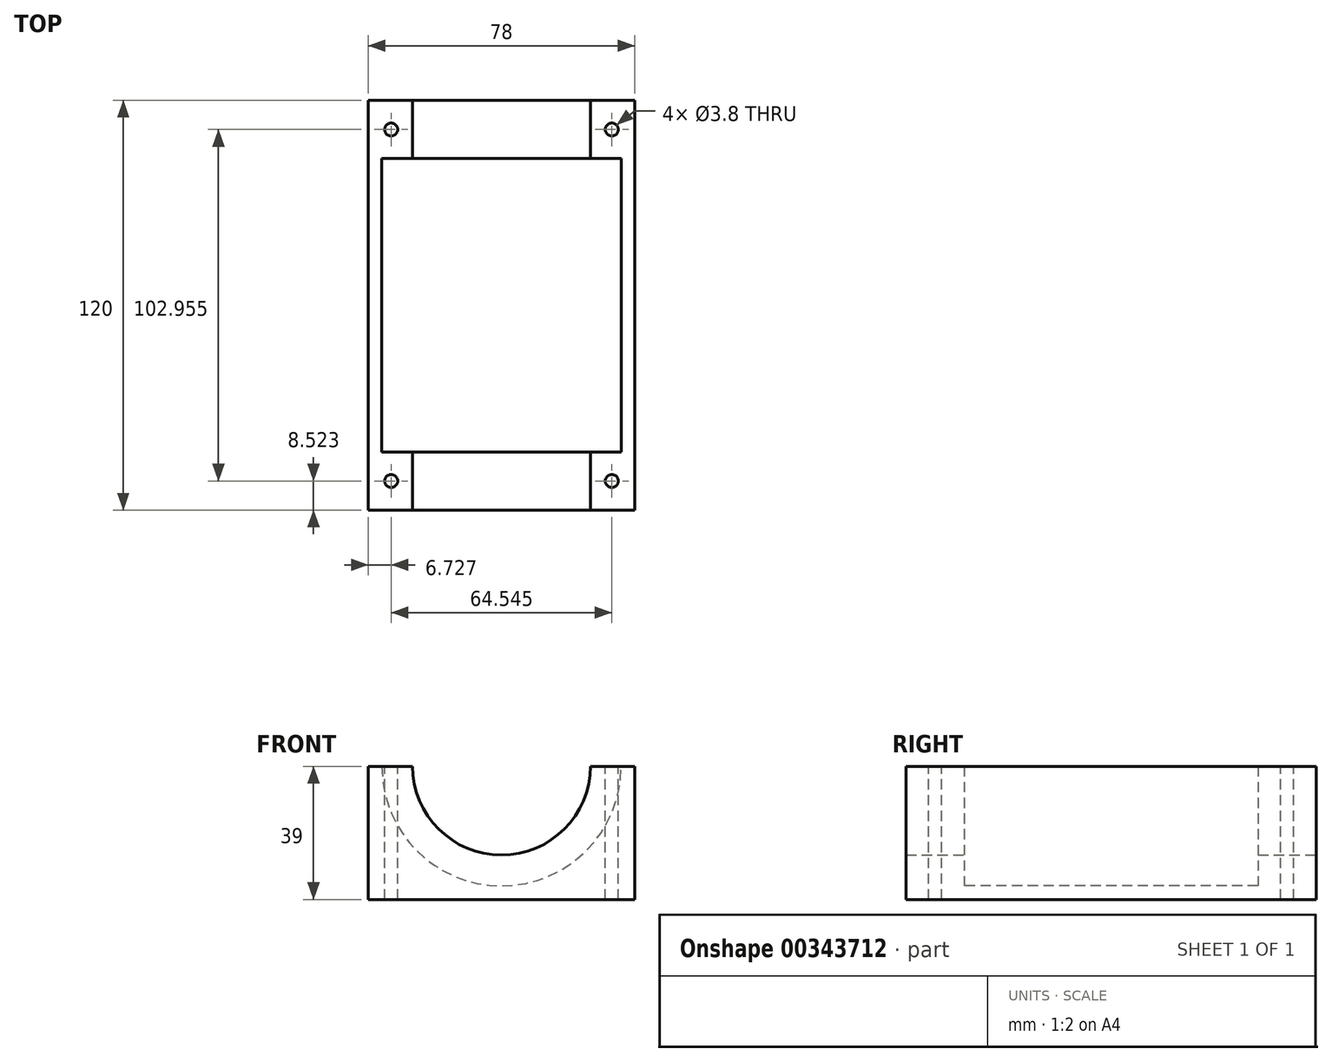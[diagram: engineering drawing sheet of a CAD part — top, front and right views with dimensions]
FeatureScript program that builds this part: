
annotation { "Feature Type Name" : "Feature", "Feature Type Description" : "" }
export const myFeature = defineFeature(function(context is Context, id is Id, definition is map)
    precondition{}
    {
        {
            var Q0;
            Q0=qCreatedBy(makeId("Front.planeOp"),FACE);
            var sketch = newSketch(context, id + "F0", { "sketchPlane" : qUnion([Q0])});
            skLineSegment(sketch, "E0.bottom", {"start": v(39, -19.5) * mm, "end": v(-39, -19.5) * mm});
            skLineSegment(sketch, "E0.left", {"start": v(39, -19.5) * mm, "end": v(39, 19.5) * mm});
            skLineSegment(sketch, "E0.right", {"start": v(-39, -19.5) * mm, "end": v(-39, 19.5) * mm});
            skPoint(sketch, "E0.middle", {"position": v(0, 0) * mm});
            skArc(sketch, "E1", {"start": v(-26, 19.5) * mm, "mid": v(0, -6.5) * mm, "end": v(26, 19.5) * mm});
            skLineSegment(sketch, "E2", {"start": v(-39, 19.5) * mm, "end": v(-26, 19.5) * mm});
            skLineSegment(sketch, "E3", {"start": v(26, 19.5) * mm, "end": v(39, 19.5) * mm});
            skSolve(sketch);
        }
        {
            var Q0;
            Q0=makeQuery(id+"F0.imprint","IMPRINT",FACE,{"disambiguationData":[TD([[makeQuery(id+"F0.imprint","IMPRINT",EDGE,{"derivedFrom":sQuery(id+"F0.wireOp",EDGE,"E0.bottom")}),-1.0]])]});
            extrude(context, id + "F1", {"entities" : qUnion([Q0]), "depth" : 60 * mm, "hasSecondDirection" : true, "secondDirectionOppositeDirection" : true, "secondDirectionDepth" : 60 * mm});
        }
        {
            var Q0;
            Q0=qCreatedBy(makeId("Front.planeOp"),FACE);
            var sketch = newSketch(context, id + "F2", { "sketchPlane" : qUnion([Q0])});
            skCircle(sketch, "E4", {"center": v(0, 19.5) * mm, "radius": 35 * mm});
            skSolve(sketch);
        }
        {
            var Q0;
            Q0=qSketchRegion(id+"F2",true);
            extrude(context, id + "F3", {"entities" : qUnion([Q0]), "operationType" : NewBodyOperationType.REMOVE, "oppositeDirection" : true, "depth" : 43 * mm, "hasSecondDirection" : true, "secondDirectionOppositeDirection" : false, "secondDirectionDepth" : 43 * mm});
        }
        {
            var Q0;
            Q0=qCreatedBy(makeId("Top.planeOp"),FACE);
            var sketch = newSketch(context, id + "F4", { "sketchPlane" : qUnion([Q0])});
            skCircle(sketch, "E5", {"center": v(-32.27, 51.48) * mm, "radius": 1.9 * mm});
            skCircle(sketch, "E6", {"center": v(32.27, 51.48) * mm, "radius": 1.9 * mm});
            skCircle(sketch, "E7", {"center": v(32.27, -51.48) * mm, "radius": 1.9 * mm});
            skCircle(sketch, "E8", {"center": v(-32.27, -51.48) * mm, "radius": 1.9 * mm});
            skSolve(sketch);
        }
        {
            var Q0;
            Q0=qSketchRegion(id+"F4",true);
            extrude(context, id + "F5", {"entities" : qUnion([Q0]), "operationType" : NewBodyOperationType.REMOVE, "oppositeDirection" : true, "depth" : 50 * mm, "hasSecondDirection" : true, "secondDirectionOppositeDirection" : false, "secondDirectionDepth" : 50 * mm});
        }
    });
